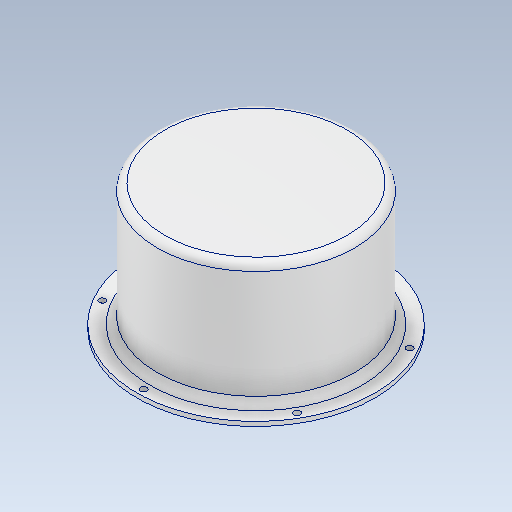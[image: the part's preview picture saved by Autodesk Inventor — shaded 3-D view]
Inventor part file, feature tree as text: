
AUTODESK INVENTOR PART (.ipt)
format: ipt  version: 2021 (Build 250183000, 183)  size: 207,872 bytes
history: native  units: mm
features: sketch x2, revolve x1, hole x1, fillet x1, projected_geometry x1
ambient origin geometry x8: Origin, YZ Plane, XZ Plane, XY Plane, X Axis, Y Axis, Z Axis, Center Point
bodies: Solid1 (feature_tree)
feature tree (6):
  revolve  "Revolution1"  [1 undecoded]
  hole  "Hole1"  [1 undecoded]
  fillet  "Fillet1"  [1 undecoded]
  sketch  "Sketch1"  dims[d3=90.0deg d5=81.5mm]
  sketch  "Sketch2"  dims[d7=9.0mm d8=5.0mm d9=45.0deg d10=16.0mm d11=3.0mm d16=4.5mm d17=8.0mm d18=60.0mm d20=360.0deg d22=4.5mm d23=10.0mm d24=9.4mm d25=2.0mm d26=90.0deg d27=13.0mm d28=20.594885mm d29=4.5mm d30=2.0mm d32=2.0mm d33=5.0mm d34=87.0mm]
  projected_geometry  "Projected Loop1"
note: 3 required parameter values undecoded (feature->parameter linkage not recoverable at this tier; creation-order binding heuristic only, values carry confidence <= 0.55)